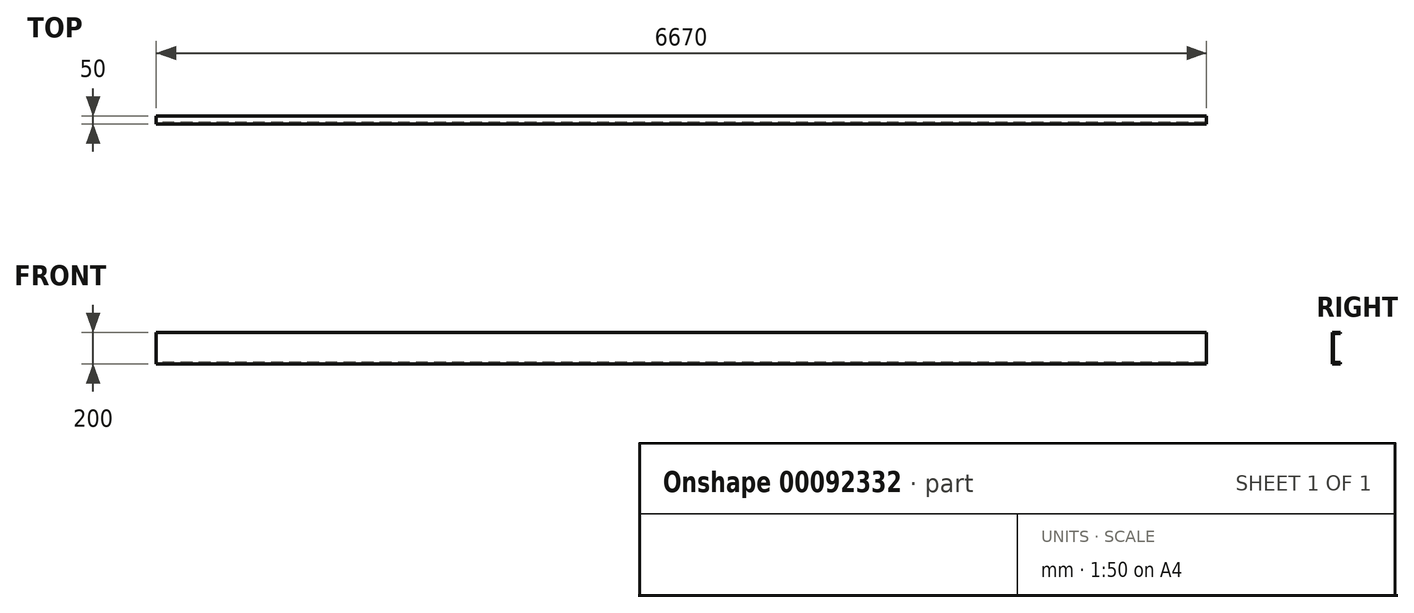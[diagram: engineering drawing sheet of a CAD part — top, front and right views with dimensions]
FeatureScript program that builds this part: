
annotation { "Feature Type Name" : "Feature", "Feature Type Description" : "" }
export const myFeature = defineFeature(function(context is Context, id is Id, definition is map)
    precondition{}
    {
        {
            var Q0;
            Q0=qCreatedBy(makeId("Right.planeOp"),FACE);
            var sketch = newSketch(context, id + "F0", { "sketchPlane" : qUnion([Q0])});
            skLineSegment(sketch, "E0", {"start": v(0, 0) * mm, "end": v(-50, 0) * mm});
            skLineSegment(sketch, "E1", {"start": v(-50, 0) * mm, "end": v(-50, 200) * mm});
            skLineSegment(sketch, "E2", {"start": v(-50, 200) * mm, "end": v(0, 200) * mm});
            skLineSegment(sketch, "E3", {"start": v(0, 200) * mm, "end": v(0, 192) * mm});
            skLineSegment(sketch, "E4", {"start": v(0, 192) * mm, "end": v(-42, 192) * mm});
            skLineSegment(sketch, "E5", {"start": v(-42, 192) * mm, "end": v(-42, 8) * mm});
            skLineSegment(sketch, "E6", {"start": v(-42, 8) * mm, "end": v(0, 8) * mm});
            skLineSegment(sketch, "E7", {"start": v(0, 8) * mm, "end": v(0, 0) * mm});
            skSolve(sketch);
        }
        {
            var Q0;
            Q0=qSketchRegion(id+"F0",true);
            extrude(context, id + "F1", {"entities" : qUnion([Q0]), "depth" : 6670 * mm});
        }
    });
